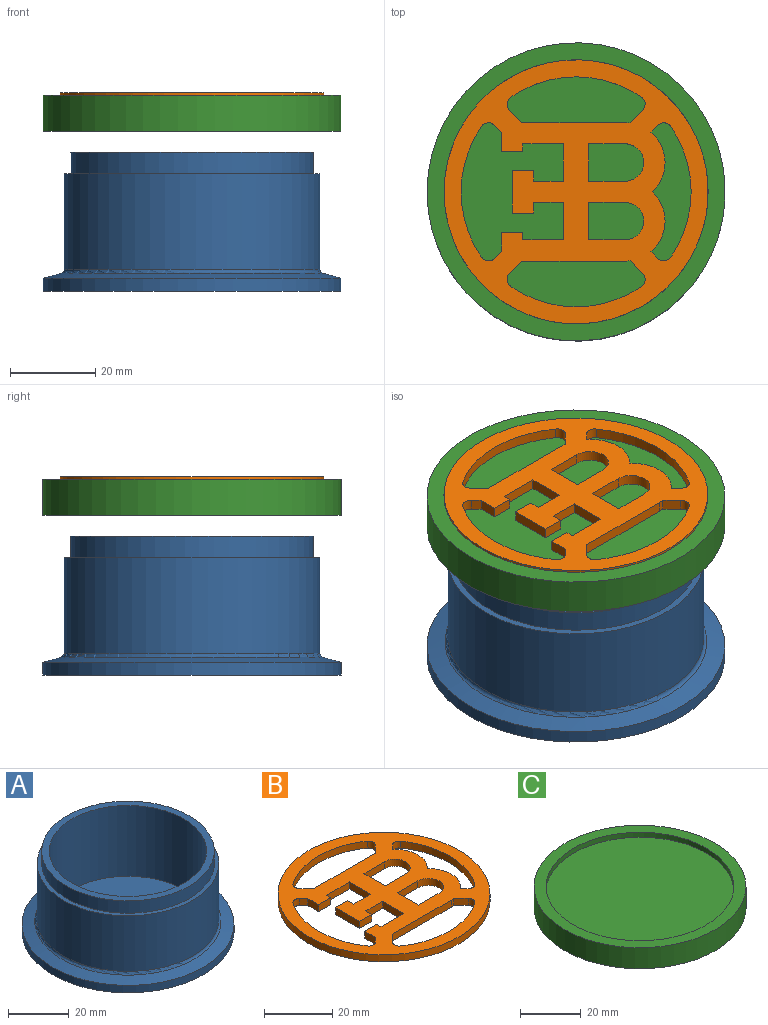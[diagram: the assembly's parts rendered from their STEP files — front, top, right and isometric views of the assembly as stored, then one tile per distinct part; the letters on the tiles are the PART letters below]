
ASSEMBLY  parts=3 mates=2
PART A: 10 faces, bbox 70x70x32.6 mm
  f0: cylinder r=30mm len=60mm, axis (0,0,-1), area 4236mm2, adj f5,f9
  f1: cone r=30mm half-angle=75deg, axis (0,0,-1), area 910.6mm2, adj f3,f9
  f2: plane 70x70mm, normal (0,0,-1), area 3848.5mm2, adj f3
  f3: cylinder r=35mm len=70mm, axis (0,0,-1), area 659.7mm2, adj f1,f2
  f4: cylinder r=28.5mm len=57mm, axis (0,0,1), area 895.4mm2, adj f5,f8
  f5: plane 60x60mm, normal (0,0,1), area 275.7mm2, adj f0,f4
  f6: plane 52x52mm, normal (0,0,1), area 2123.7mm2, adj f7
  f7: cylinder r=26mm len=52mm, axis (0,0,-1), area 4668.8mm2, adj f6,f8
  f8: plane 57x57mm, normal (0,0,1), area 428mm2, adj f4,f7
  f9: torus R=31mm, axis (0,0,-1), area 248.9mm2, adj f0,f1
PART B: 54 faces, bbox 62x62x2.5 mm
  f0: plane 2.5x1.66mm, normal (-0.71,-0.71,0), area 5.9mm2, adj f6,f8,f16,f49
  f1: plane 2.5x1.59mm, normal (0.71,-0.71,0), area 5.6mm2, adj f6,f8,f17,f53
  f2: plane 2.96x2.96mm, normal (-0.71,0.71,0), area 10.5mm2, adj f6,f8,f28,f46
  f3: cylinder r=27mm len=30.69mm, axis (0,0,-1), area 81.6mm2, adj f6,f8,f50,f51
  f4: cylinder r=27mm len=30.69mm, axis (0,0,-1), area 81.6mm2, adj f6,f8,f52,f53
  f5: cylinder r=27mm len=30.69mm, axis (0,0,-1), area 81.6mm2, adj f6,f8,f46,f47
  f6: plane 62x62mm, normal (0,0,-1), area 1601mm2, adj f0,f1,f2,f3,f4,f5,f7,f9
  f7: plane 2.89x2.89mm, normal (0.71,0.71,0), area 10.2mm2, adj f6,f8,f15,f47
  f8: plane 62x62mm, normal (0,0,1), area 1601mm2, adj f0,f1,f2,f3,f4,f5,f7,f9
  f9: cylinder r=27mm len=30.69mm, axis (0,0,-1), area 81.6mm2, adj f6,f8,f48,f49
  f10: cylinder r=31mm len=62mm, axis (0,0,-1), area 486.9mm2, adj f6,f8
  f11: plane 2.5x1.59mm, normal (0.71,0.71,0), area 5.6mm2, adj f6,f8,f18,f52
  f12: plane 2.96x2.96mm, normal (-0.71,-0.71,0), area 10.5mm2, adj f6,f8,f19,f51
  f13: plane 2.89x2.89mm, normal (0.71,-0.71,0), area 10.2mm2, adj f6,f8,f20,f50
  f14: plane 2.5x1.66mm, normal (-0.71,0.71,0), area 5.9mm2, adj f6,f8,f21,f48
  f15: plane 24.23x2.5mm, normal (0,1,0), area 60.6mm2, adj f6,f7,f8,f28
  f16: plane 4.45x2.5mm, normal (-1,0,0), area 11.1mm2, adj f0,f6,f8,f42
  f17: cylinder r=9.38mm len=14.04mm, axis (0,0,-1), area 39.7mm2, adj f1,f6,f8,f18
  f18: cylinder r=9.38mm len=14.04mm, axis (0,0,-1), area 39.7mm2, adj f6,f8,f11,f17
  f19: cylinder r=9.38mm len=2.5mm, axis (0,0,-1), area 2.9mm2, adj f6,f8,f12,f20
  f20: plane 24.23x2.5mm, normal (0,-1,0), area 60.6mm2, adj f6,f8,f13,f19
  f21: plane 4.45x2.5mm, normal (-1,0,0), area 11.1mm2, adj f6,f8,f14,f45
  f22: plane 9.5x2.5mm, normal (0,-1,0), area 23.8mm2, adj f6,f8,f29,f43
  f23: cylinder r=4.38mm len=8.76mm, axis (0,0,-1), area 34.4mm2, adj f6,f8,f35,f36
  f24: plane 2.5x2.5mm, normal (1,0,0), area 6.2mm2, adj f6,f8,f25,f33
  f25: plane 7x2.5mm, normal (0,-1,0), area 17.5mm2, adj f6,f8,f24,f26
  f26: plane 8.76x2.5mm, normal (-1,0,0), area 21.9mm2, adj f6,f8,f25,f27
  f27: plane 9.5x2.5mm, normal (0,1,0), area 23.8mm2, adj f6,f8,f26,f44
  f28: cylinder r=9.38mm len=2.5mm, axis (0,0,-1), area 2.9mm2, adj f2,f6,f8,f15
  f29: plane 8.76x2.5mm, normal (-1,0,0), area 21.9mm2, adj f6,f8,f22,f30
  f30: plane 7x2.5mm, normal (0,1,0), area 17.5mm2, adj f6,f8,f29,f31
  f31: plane 2.5x2.5mm, normal (1,0,0), area 6.3mm2, adj f6,f8,f30,f40
  f32: plane 8.5x2.5mm, normal (0,-1,0), area 21.2mm2, adj f6,f8,f34,f38
  f33: plane 5x2.5mm, normal (0,-1,0), area 12.5mm2, adj f6,f8,f24,f41
  f34: plane 8.76x2.5mm, normal (1,0,0), area 21.9mm2, adj f6,f8,f32,f39
  f35: plane 8.5x2.5mm, normal (0,1,0), area 21.2mm2, adj f6,f8,f23,f37
  f36: plane 8.5x2.5mm, normal (0,-1,0), area 21.2mm2, adj f6,f8,f23,f37
  f37: plane 8.76x2.5mm, normal (1,0,0), area 21.9mm2, adj f6,f8,f35,f36
  f38: cylinder r=4.38mm len=8.76mm, axis (0,0,-1), area 34.4mm2, adj f6,f8,f32,f39
  f39: plane 8.5x2.5mm, normal (0,1,0), area 21.2mm2, adj f6,f8,f34,f38
  f40: plane 5x2.5mm, normal (0,1,0), area 12.5mm2, adj f6,f8,f31,f41
  f41: plane 10x2.5mm, normal (-1,0,0), area 25mm2, adj f6,f8,f33,f40
  f42: plane 5x2.5mm, normal (0,-1,0), area 12.5mm2, adj f6,f8,f16,f43
  f43: plane 2.5x1.75mm, normal (1,0,0), area 4.4mm2, adj f6,f8,f22,f42
  f44: plane 2.5x1.75mm, normal (1,0,0), area 4.4mm2, adj f6,f8,f27,f45
  f45: plane 5x2.5mm, normal (0,1,0), area 12.5mm2, adj f6,f8,f21,f44
  f46: cylinder r=2mm len=3.06mm, axis (0,0,-1), area 8.8mm2, adj f2,f5,f6,f8
  f47: cylinder r=2mm len=3.06mm, axis (0,0,-1), area 8.8mm2, adj f5,f6,f7,f8
  f48: cylinder r=2mm len=3.06mm, axis (0,0,-1), area 8.8mm2, adj f6,f8,f9,f14
  f49: cylinder r=2mm len=3.06mm, axis (0,0,-1), area 8.8mm2, adj f0,f6,f8,f9
  f50: cylinder r=2mm len=3.06mm, axis (0,0,-1), area 8.8mm2, adj f3,f6,f8,f13
  f51: cylinder r=2mm len=3.06mm, axis (0,0,-1), area 8.8mm2, adj f3,f6,f8,f12
  f52: cylinder r=2mm len=3.06mm, axis (0,0,-1), area 8.8mm2, adj f4,f6,f8,f11
  f53: cylinder r=2mm len=3.06mm, axis (0,0,-1), area 8.8mm2, adj f1,f4,f6,f8
PART C: 7 faces, bbox 70x70x8.5 mm
  f0: plane 65x65mm, normal (0,0,-1), area 3318.3mm2, adj f1
  f1: cylinder r=32.5mm len=65mm, axis (0,0,-1), area 918.9mm2, adj f0,f2
  f2: plane 70x70mm, normal (0,0,-1), area 530.1mm2, adj f1,f3
  f3: cylinder r=35mm len=70mm, axis (0,0,-1), area 1869.2mm2, adj f2,f4
  f4: plane 70x70mm, normal (0,0,1), area 829.4mm2, adj f3,f5
  f5: cylinder r=31mm len=62mm, axis (0,0,1), area 389.6mm2, adj f4,f6
  f6: plane 62x62mm, normal (0,0,1), area 3019.1mm2, adj f5
PLACE A t=(-27.67,-25.76,-30.97)mm fixed
PLACE B t=(-27.67,-25.76,13.03)mm
PLACE C t=(-27.67,-25.76,6.53)mm
MATE slider C.f1 <-> A.f0  axis (0,0,1) through (-27.67,-25.76,13.03)mm
MATE fastened B.f3 <-> C.f1  axis (0,0,-1) through (-27.67,-25.76,13.03)mm
